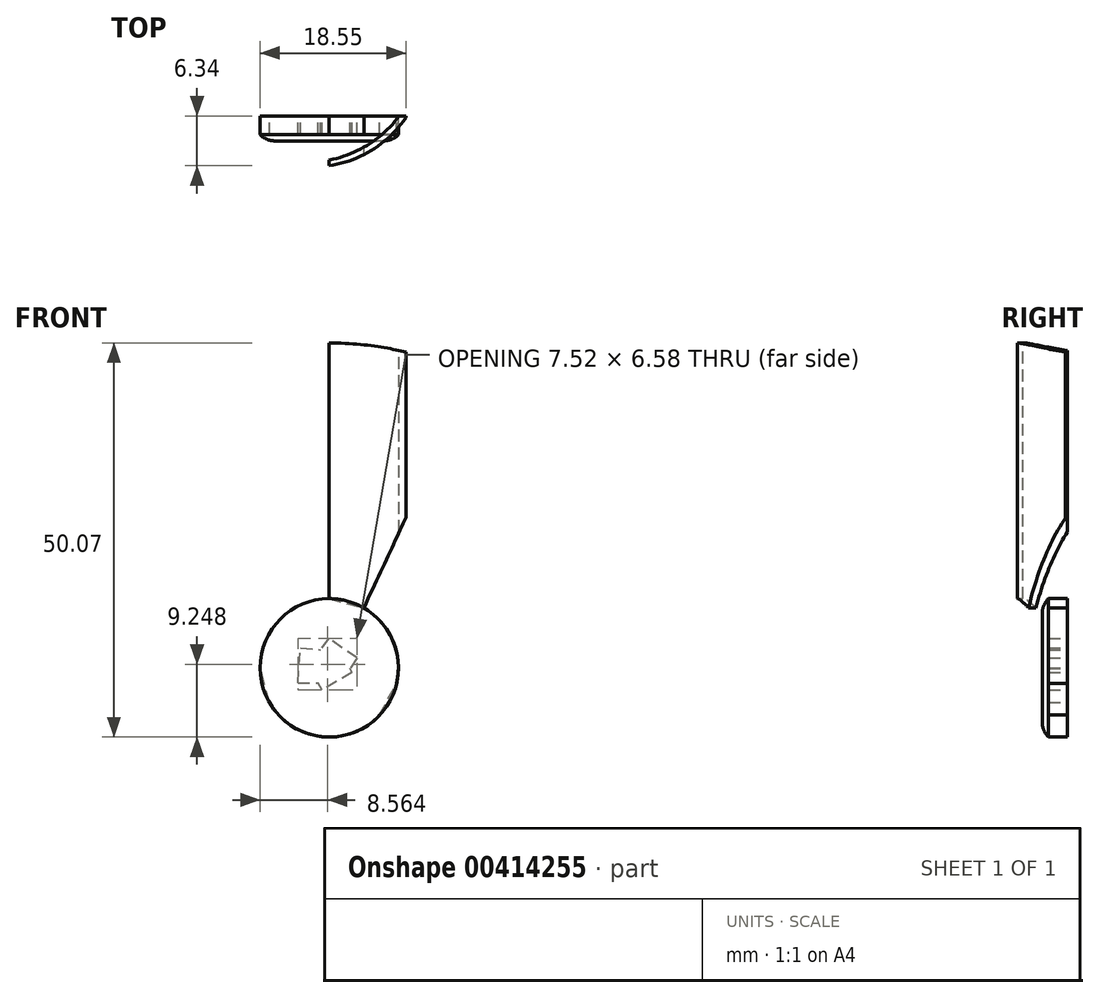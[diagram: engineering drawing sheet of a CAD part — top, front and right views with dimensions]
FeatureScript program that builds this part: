
annotation { "Feature Type Name" : "Feature", "Feature Type Description" : "" }
export const myFeature = defineFeature(function(context is Context, id is Id, definition is map)
    precondition{}
    {
        {
            var Q0;
            Q0=qCreatedBy(makeId("Front.planeOp"),FACE);
            var sketch = newSketch(context, id + "F0", { "sketchPlane" : qUnion([Q0])});
            skCircle(sketch, "E0", {"center": v(0, 0) * mm, "radius": 41.28 * mm});
            skCircle(sketch, "E1", {"center": v(0, 0) * mm, "radius": 8.79 * mm});
            skCircle(sketch, "E2.cCircle", {"center": v(0, 0) * mm, "radius": 41.28 * mm, "construction": true});
            skLineSegment(sketch, "E3", {"start": v(0, 41.28) * mm, "end": v(0, 8.79) * mm});
            skLineSegment(sketch, "E4", {"start": v(-35.75, -20.64) * mm, "end": v(-7.61, -4.4) * mm});
            skLineSegment(sketch, "E5", {"start": v(40.2, -9.37) * mm, "end": v(8.56, -2) * mm});
            skLineSegment(sketch, "E6", {"start": v(-7.61, -4.4) * mm, "end": v(-8.79, 0) * mm});
            skLineSegment(sketch, "E7", {"start": v(-8.79, 0) * mm, "end": v(-21.44, -1.1) * mm});
            skLineSegment(sketch, "E8", {"start": v(-21.44, -1.1) * mm, "end": v(-39.61, -11.6) * mm});
            skLineSegment(sketch, "E9", {"start": v(6.41, -6) * mm, "end": v(8.56, -2) * mm});
            skLineSegment(sketch, "E10", {"start": v(6.41, -6) * mm, "end": v(16.4, -13.85) * mm});
            skLineSegment(sketch, "E11", {"start": v(16.4, -13.85) * mm, "end": v(36.84, -18.61) * mm});
            skLineSegment(sketch, "E12", {"start": v(0, 8.79) * mm, "end": v(4.4, 7.61) * mm});
            skLineSegment(sketch, "E13", {"start": v(4.4, 7.61) * mm, "end": v(9.76, 19.12) * mm});
            skLineSegment(sketch, "E14", {"start": v(9.76, 19.12) * mm, "end": v(9.76, 40.1) * mm});
            skLineSegment(sketch, "E15", {"start": v(0, 0) * mm, "end": v(-35.75, -20.64) * mm});
            skSolve(sketch);
        }
        {
            var Q0;
            {var subQ1=sQuery(id+"F0.wireOp",EDGE,"E3");Q0=makeQuery(id+"F0.imprint","IMPRINT",FACE,{"disambiguationData":[TD([[makeQuery(id+"F0.imprint","IMPRINT",EDGE,{"derivedFrom":subQ1}),1.0]])]});}
            var Q1;
            {var subQ1=sQuery(id+"F0.wireOp",EDGE,"E7");Q1=makeQuery(id+"F0.imprint","IMPRINT",FACE,{"disambiguationData":[TD([[makeQuery(id+"F0.imprint","IMPRINT",EDGE,{"derivedFrom":subQ1}),1.0]])]});}
            var Q2;
            {var subQ1=sQuery(id+"F0.wireOp",EDGE,"E5");Q2=makeQuery(id+"F0.imprint","IMPRINT",FACE,{"disambiguationData":[TD([[makeQuery(id+"F0.imprint","IMPRINT",EDGE,{"derivedFrom":subQ1}),1.0]])]});}
            extrude(context, id + "F1", {"entities" : qUnion([Q0, Q1, Q2]), "depth" : 6.35 * mm});
        }
        {
            var Q0;
            Q0=qCreatedBy(makeId("Top.planeOp"),FACE);
            cPlane(context, id + "F2", {"entities" : qUnion([Q0]), "cplaneType" : CPlaneType.OFFSET, "offset" : 41.27 * mm, "width" : 152.4 * mm, "height" : 152.4 * mm});
        }
        {
            var Q0;
            Q0=qCreatedBy(id+"F2.planeOp",FACE);
            var sketch = newSketch(context, id + "F3", { "sketchPlane" : qUnion([Q0])});
            skArc(sketch, "E16", {"start": v(0, -6.34) * mm, "mid": v(5.62, -4.22) * mm, "end": v(9.9, 0) * mm});
            skLineSegment(sketch, "E17", {"start": v(9.9, 0) * mm, "end": v(8.9, 0) * mm});
            skArc(sketch, "E18", {"start": v(0, -5.6) * mm, "mid": v(4.98, -3.64) * mm, "end": v(8.9, 0) * mm});
            skLineSegment(sketch, "E19", {"start": v(0, -6.34) * mm, "end": v(0, -5.6) * mm});
            skLineSegment(sketch, "E20.bottom", {"start": v(9.76, -6.35) * mm, "end": v(0, -6.35) * mm});
            skLineSegment(sketch, "E20.top", {"start": v(9.76, 0) * mm, "end": v(0, 0) * mm});
            skLineSegment(sketch, "E20.left", {"start": v(9.76, -6.35) * mm, "end": v(9.76, 0) * mm});
            skLineSegment(sketch, "E20.right", {"start": v(0, -6.35) * mm, "end": v(0, 0) * mm});
            skSolve(sketch);
        }
        {
            var Q0;
            {var subQ5=sQuery(id+"F3.wireOp",EDGE,"E20.bottom");Q0=makeQuery(id+"F3.imprint","IMPRINT",FACE,{"disambiguationData":[TD([[makeQuery(id+"F3.imprint","IMPRINT",EDGE,{"derivedFrom":subQ5}),-1.0]])]});}
            var Q1;
            {var subQ0=sQuery(id+"F3.wireOp",EDGE,"E18");Q1=makeQuery(id+"F3.imprint","IMPRINT",FACE,{"disambiguationData":[TD([[makeQuery(id+"F3.imprint","IMPRINT",EDGE,{"derivedFrom":subQ0}),1.0]])]});}
            extrude(context, id + "F4", {"entities" : qUnion([Q0, Q1]), "operationType" : NewBodyOperationType.REMOVE, "oppositeDirection" : true, "depth" : 34.85 * mm});
        }
        {
            var Q0;
            Q0=makeQuery(id+"F1.opExtrude","SWEPT_BODY",BODY,{"disambiguationData":[OSD([sQuery(id+"F0.wireOp",EDGE,"E0"),sQuery(id+"F0.wireOp",EDGE,"E1"),sQuery(id+"F0.wireOp",EDGE,"E7"),sQuery(id+"F0.wireOp",EDGE,"E8"),sQuery(id+"F0.wireOp",EDGE,"E15")])]});
            var Q1;
            Q1=makeQuery(id+"F1.opExtrude","SWEPT_BODY",BODY,{"disambiguationData":[OSD([sQuery(id+"F0.wireOp",EDGE,"E0"),sQuery(id+"F0.wireOp",EDGE,"E1"),sQuery(id+"F0.wireOp",EDGE,"E5"),sQuery(id+"F0.wireOp",EDGE,"E10"),sQuery(id+"F0.wireOp",EDGE,"E11")])]});
            deleteBodies(context, id + "F5", {"entities" : qUnion([Q0, Q1])});
        }
        {
            var Q0;
            Q0=qCreatedBy(makeId("Front.planeOp"),FACE);
            cPlane(context, id + "F6", {"entities" : qUnion([Q0]), "cplaneType" : CPlaneType.OFFSET, "offset" : 2.38 * mm, "width" : 152.4 * mm, "height" : 152.4 * mm});
        }
        {
            var Q0;
            Q0=qCreatedBy(id+"F6.planeOp",FACE);
            var sketch = newSketch(context, id + "F7", { "sketchPlane" : qUnion([Q0])});
            skCircle(sketch, "E21", {"center": v(0, 0) * mm, "radius": 8.79 * mm});
            skSolve(sketch);
        }
        {
            var Q0;
            Q0=makeQuery(id+"F7.imprint","IMPRINT",FACE,{"disambiguationData":[TD([[makeQuery(id+"F7.imprint","IMPRINT",EDGE,{"derivedFrom":sQuery(id+"F7.wireOp",EDGE,"E21")}),1.0]])]});
            extrude(context, id + "F8", {"entities" : qUnion([Q0]), "depth" : 0.8 * mm});
        }
        {
            var Q0;
            Q0=makeQuery(id+"F8.opExtrude","CAP_FACE",FACE,{"disambiguationData":[OSD([sQuery(id+"F7.wireOp",EDGE,"E21")])],"isStart":false});
            fillet(context, id + "F9", {"entities" : qUnion([Q0]), "radius" : 2.54 * mm, "tangentPropagation" : true, "allowEdgeOverflow" : false});
        }
        {
            var Q0;
            {var subQ3=sQuery(id+"F0.wireOp",EDGE,"E6");Q0=makeQuery(id+"F0.imprint","IMPRINT",FACE,{"disambiguationData":[TD([[makeQuery(id+"F0.imprint","IMPRINT",EDGE,{"derivedFrom":subQ3}),-1.0]])]});}
            extrude(context, id + "F10", {"entities" : qUnion([Q0]), "depth" : 2.38 * mm});
        }
        {
            var Q0;
            Q0=makeQuery(id+"F10.opExtrude","CAP_FACE",FACE,{"disambiguationData":[OSD([sQuery(id+"F0.wireOp",EDGE,"E1"),sQuery(id+"F0.wireOp",EDGE,"E6"),sQuery(id+"F0.wireOp",EDGE,"E9"),sQuery(id+"F0.wireOp",EDGE,"E12")])],"isStart":true});
            var sketch = newSketch(context, id + "F11", { "sketchPlane" : qUnion([Q0])});
            skCircle(sketch, "E22.cCircle", {"center": v(0, 0) * mm, "radius": 8.79 * mm, "construction": true});
            skPoint(sketch, "E22.cCircle.perimeterSnap0", {"position": v(-2.2, 8.2) * mm});
            skPoint(sketch, "E22.0.startSnap0", {"position": v(-2.2, 8.2) * mm});
            skLineSegment(sketch, "E23", {"start": v(-1.01, -1.7) * mm, "end": v(0, 0) * mm});
            skLineSegment(sketch, "E24", {"start": v(0, 0) * mm, "end": v(-1.71, 2.5) * mm});
            skLineSegment(sketch, "E25", {"start": v(3.82, 0.3) * mm, "end": v(0, 0) * mm});
            skLineSegment(sketch, "E26", {"start": v(-1.71, 2.5) * mm, "end": v(-3.54, 1.25) * mm});
            skLineSegment(sketch, "E27", {"start": v(-1.71, 2.5) * mm, "end": v(0.1, 3.75) * mm});
            skLineSegment(sketch, "E28", {"start": v(-3.54, 1.25) * mm, "end": v(-2.1, -0.85) * mm});
            skPoint(sketch, "E28.endSnap0", {"position": v(-0.5, -0.85) * mm});
            skLineSegment(sketch, "E29", {"start": v(-1.01, -1.7) * mm, "end": v(-2.91, -0.56) * mm});
            skLineSegment(sketch, "E30", {"start": v(-1.01, -1.7) * mm, "end": v(0.88, -2.83) * mm});
            skLineSegment(sketch, "E31", {"start": v(-2.91, -0.56) * mm, "end": v(-1.6, 1.63) * mm});
            skLineSegment(sketch, "E32", {"start": v(0.1, 3.75) * mm, "end": v(5.03, -3.42) * mm});
            skLineSegment(sketch, "E33", {"start": v(0.88, -2.83) * mm, "end": v(2.2, -0.64) * mm});
            skLineSegment(sketch, "E34", {"start": v(3.82, 0.3) * mm, "end": v(3.99, -1.9) * mm});
            skLineSegment(sketch, "E35", {"start": v(3.82, 0.3) * mm, "end": v(3.64, 2.5) * mm});
            skLineSegment(sketch, "E36", {"start": v(3.99, -1.9) * mm, "end": v(1.44, -1.9) * mm});
            skLineSegment(sketch, "E37", {"start": v(3.64, 2.5) * mm, "end": v(1.1, 2.3) * mm});
            skSolve(sketch);
        }
        {
            var Q0;
            {var subQ0=sQuery(id+"F11.wireOp",EDGE,"E35");Q0=makeQuery(id+"F11.imprint","IMPRINT",FACE,{"disambiguationData":[TD([[makeQuery(id+"F11.imprint","IMPRINT",EDGE,{"derivedFrom":subQ0}),1.0]])]});}
            var Q1;
            {var subQ0=sQuery(id+"F11.wireOp",EDGE,"E37");var subQ1=sQuery(id+"F11.wireOp",EDGE,"E32");var subQ2=makeQuery(id+"F11.imprint","INTERSECT",VERTEX,{"derivedFrom":[subQ1,subQ0]});Q1=makeQuery(id+"F11.imprint","IMPRINT",FACE,{"disambiguationData":[TD([[makeQuery(id+"F11.imprint","IMPRINT",EDGE,{"disambiguationData":[TD([[subQ2,-1.0]])],"derivedFrom":subQ1}),1.0]])]});}
            var Q2;
            {var subQ0=sQuery(id+"F11.wireOp",EDGE,"E34");Q2=makeQuery(id+"F11.imprint","IMPRINT",FACE,{"disambiguationData":[TD([[makeQuery(id+"F11.imprint","IMPRINT",EDGE,{"derivedFrom":subQ0}),-1.0]])]});}
            var Q3;
            {var subQ5=sQuery(id+"F11.wireOp",EDGE,"E36");Q3=makeQuery(id+"F11.imprint","IMPRINT",FACE,{"disambiguationData":[TD([[makeQuery(id+"F11.imprint","IMPRINT",EDGE,{"derivedFrom":subQ5}),-1.0]])]});}
            var Q4;
            {var subQ0=sQuery(id+"F11.wireOp",EDGE,"E32");var subQ1=sQuery(id+"F11.wireOp",EDGE,"E25");var subQ2=makeQuery(id+"F11.imprint","INTERSECT",VERTEX,{"derivedFrom":[subQ1,subQ0]});Q4=makeQuery(id+"F11.imprint","IMPRINT",FACE,{"disambiguationData":[TD([[makeQuery(id+"F11.imprint","IMPRINT",EDGE,{"disambiguationData":[TD([[subQ2,-1.0]])],"derivedFrom":subQ1}),-1.0]])]});}
            var Q5;
            {var subQ0=sQuery(id+"F11.wireOp",EDGE,"E32");var subQ1=sQuery(id+"F11.wireOp",EDGE,"E31");var subQ2=makeQuery(id+"F11.imprint","INTERSECT",VERTEX,{"derivedFrom":[subQ1,subQ0]});Q5=makeQuery(id+"F11.imprint","IMPRINT",FACE,{"disambiguationData":[TD([[makeQuery(id+"F11.imprint","IMPRINT",EDGE,{"disambiguationData":[TD([[subQ2,1.0]])],"derivedFrom":subQ1}),-1.0]])]});}
            var Q6;
            {var subQ4=sQuery(id+"F11.wireOp",EDGE,"E23");Q6=makeQuery(id+"F11.imprint","IMPRINT",FACE,{"disambiguationData":[TD([[makeQuery(id+"F11.imprint","IMPRINT",EDGE,{"derivedFrom":subQ4}),-1.0]])]});}
            var Q7;
            {var subQ3=sQuery(id+"F11.wireOp",EDGE,"E23");Q7=makeQuery(id+"F11.imprint","IMPRINT",FACE,{"disambiguationData":[TD([[makeQuery(id+"F11.imprint","IMPRINT",EDGE,{"derivedFrom":subQ3}),1.0]])]});}
            var Q8;
            {var subQ0=sQuery(id+"F11.wireOp",EDGE,"E26");Q8=makeQuery(id+"F11.imprint","IMPRINT",FACE,{"disambiguationData":[TD([[makeQuery(id+"F11.imprint","IMPRINT",EDGE,{"derivedFrom":subQ0}),1.0]])]});}
            var Q9;
            {var subQ0=sQuery(id+"F11.wireOp",EDGE,"E27");Q9=makeQuery(id+"F11.imprint","IMPRINT",FACE,{"disambiguationData":[TD([[makeQuery(id+"F11.imprint","IMPRINT",EDGE,{"derivedFrom":subQ0}),-1.0]])]});}
            extrude(context, id + "F12", {"entities" : qUnion([Q0, Q1, Q2, Q3, Q4, Q5, Q6, Q7, Q8, Q9]), "operationType" : NewBodyOperationType.REMOVE, "oppositeDirection" : true, "depth" : 2.38 * mm});
        }
    });
